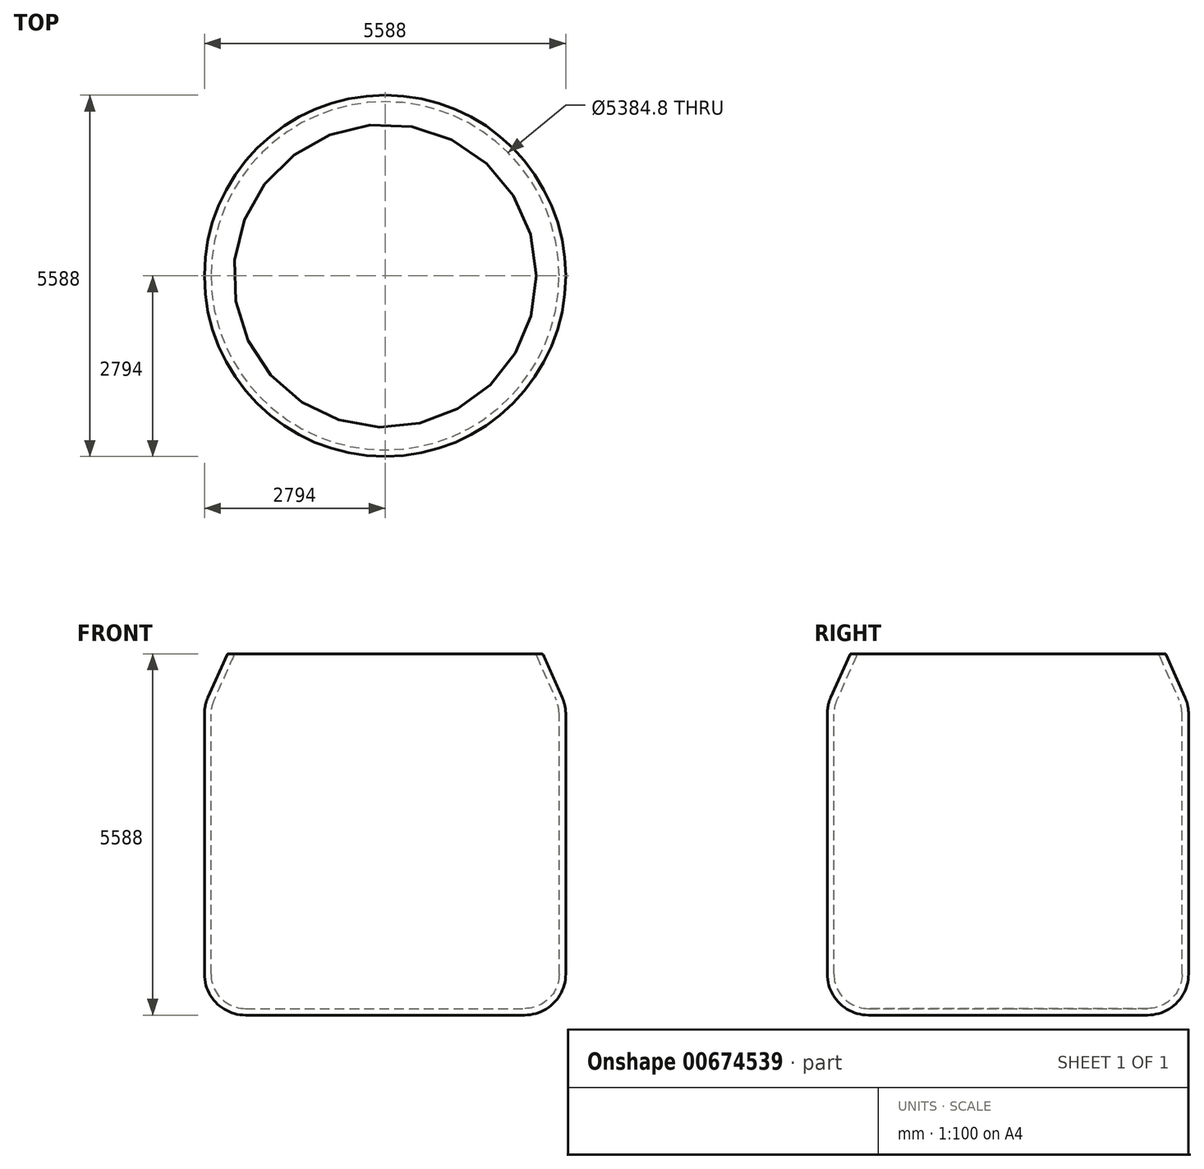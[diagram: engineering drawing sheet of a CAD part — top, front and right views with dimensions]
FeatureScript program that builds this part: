
annotation { "Feature Type Name" : "Feature", "Feature Type Description" : "" }
export const myFeature = defineFeature(function(context is Context, id is Id, definition is map)
    precondition{}
    {
        {
            var Q0;
            Q0=qCreatedBy(makeId("Front.planeOp"),FACE);
            var sketch = newSketch(context, id + "F0", { "sketchPlane" : qUnion([Q0])});
            skLineSegment(sketch, "E0", {"start": v(-2438.4, 2895.31) * mm, "end": v(-2794, 2096.62) * mm});
            skLineSegment(sketch, "E1", {"start": v(-2794, 2096.62) * mm, "end": v(-2794, -2692.69) * mm});
            skLineSegment(sketch, "E2", {"start": v(-2794, -2692.69) * mm, "end": v(0, -2692.69) * mm});
            skLineSegment(sketch, "E3", {"start": v(0, -2692.69) * mm, "end": v(0, 0) * mm});
            skLineSegment(sketch, "E4", {"start": v(0, 2895.31) * mm, "end": v(-2438.4, 2895.31) * mm});
            skLineSegment(sketch, "E5", {"start": v(0, 2895.31) * mm, "end": v(0, 0) * mm});
            skSolve(sketch);
        }
        {
            var Q0;
            Q0=makeQuery(id+"F0.imprint","IMPRINT",FACE,{"disambiguationData":[TD([[makeQuery(id+"F0.imprint","IMPRINT",EDGE,{"derivedFrom":sQuery(id+"F0.wireOp",EDGE,"E0")}),1.0]])]});
            var Q1;
            Q1=sQuery(id+"F0.wireOp",EDGE,"E5");
            revolve(context, id + "F1", {"entities" : qUnion([Q0]), "axis" : qUnion([Q1]), "revolveType" : RevolveType.FULL});
        }
        {
            var Q0;
            Q0=makeQuery(id+"F1.opRevolve","SWEPT_EDGE",EDGE,{"disambiguationData":[OSD([sQuery(id+"F0.wireOp",EDGE,"E1"),sQuery(id+"F0.wireOp",EDGE,"E2")])]});
            var Q1;
            Q1=makeQuery(id+"F1.opRevolve","SWEPT_EDGE",EDGE,{"disambiguationData":[OSD([sQuery(id+"F0.wireOp",EDGE,"E0"),sQuery(id+"F0.wireOp",EDGE,"E1")])]});
            fillet(context, id + "F2", {"entities" : qUnion([Q0, Q1]), "radius" : 635 * mm, "tangentPropagation" : true, "allowEdgeOverflow" : false});
        }
        {
            var Q0;
            Q0=makeQuery(id+"F1.opRevolve","SWEPT_FACE",FACE,{"disambiguationData":[OSD([sQuery(id+"F0.wireOp",EDGE,"E4")])]});
            shell(context, id + "F3", {"entities" : qUnion([Q0]), "thickness" : 101.6 * mm});
        }
        {
            var Q0;
            Q0=makeQuery(id+"F3.opShell","OFFSET_EDGE",EDGE,{"disambiguationData":[OSD([sQuery(id+"F0.wireOp",EDGE,"E0"),sQuery(id+"F0.wireOp",EDGE,"E4")])]});
            var Q1;
            Q1=makeQuery(id+"F1.opRevolve","SWEPT_EDGE",EDGE,{"disambiguationData":[OSD([sQuery(id+"F0.wireOp",EDGE,"E0"),sQuery(id+"F0.wireOp",EDGE,"E4")])]});
            fillet(context, id + "F4", {"entities" : qUnion([Q0, Q1]), "radius" : 25.4 * mm, "tangentPropagation" : true, "allowEdgeOverflow" : false});
        }
    });
